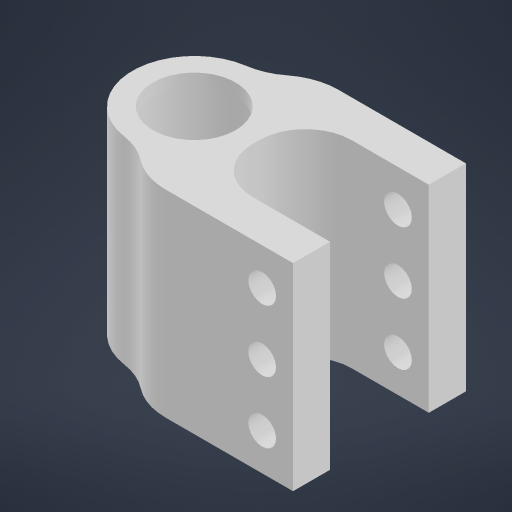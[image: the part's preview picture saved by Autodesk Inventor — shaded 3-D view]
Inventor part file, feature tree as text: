
AUTODESK INVENTOR PART (.ipt)
format: ipt  version: 2024.1 (Build 281209000, 209)  size: 272,896 bytes
history: native  units: mm
features: fillet x6, extrude x4, sketch x3
ambient origin geometry x8: Origin, YZ Plane, XZ Plane, XY Plane, X Axis, Y Axis, Z Axis, Center Point
bodies: Solid1 (feature_tree)
feature tree (13):
  sketch  "Sketch1"  dims[d0=13.4mm d1=15.4mm]
  extrude  "Extrusion1"  Depth=15.4mm
  extrude  "Extrusion2"  Depth=2.0mm TaperAngle=0.0deg
  extrude  "Extrusion3"  Depth=10.0mm
  fillet  "Fillet2"  Radius=62.5mm
  extrude  "Extrusion7"  Depth=10.0mm
  fillet  "Fillet5"  Radius=4.5mm
  fillet  "Fillet6"  Radius=10.0mm
  fillet  "Fillet7"  Radius=30.0mm
  fillet  "Fillet3"  Radius=20.0mm
  fillet  "Fillet4"  Radius=20.0mm
  sketch  "Sketch2"  dims[d3=2.0mm d4=0.0mm d5=30.0mm d6=0.0mm]
  sketch  "Sketch4"  dims[d7=3.5mm d8=5.0mm d9=62.5mm d10=0.0mm d31=7.5mm d32=4.5mm d33=10.0mm d35=30.0mm d36=0.0mm d37=20.0mm d38=20.0mm d39=6.0mm d40=5.0mm d41=5.0mm d42=7.5mm d43=2.0mm d46=16.0mm d47=10.0mm d48=10.0mm d49=10.0mm]
